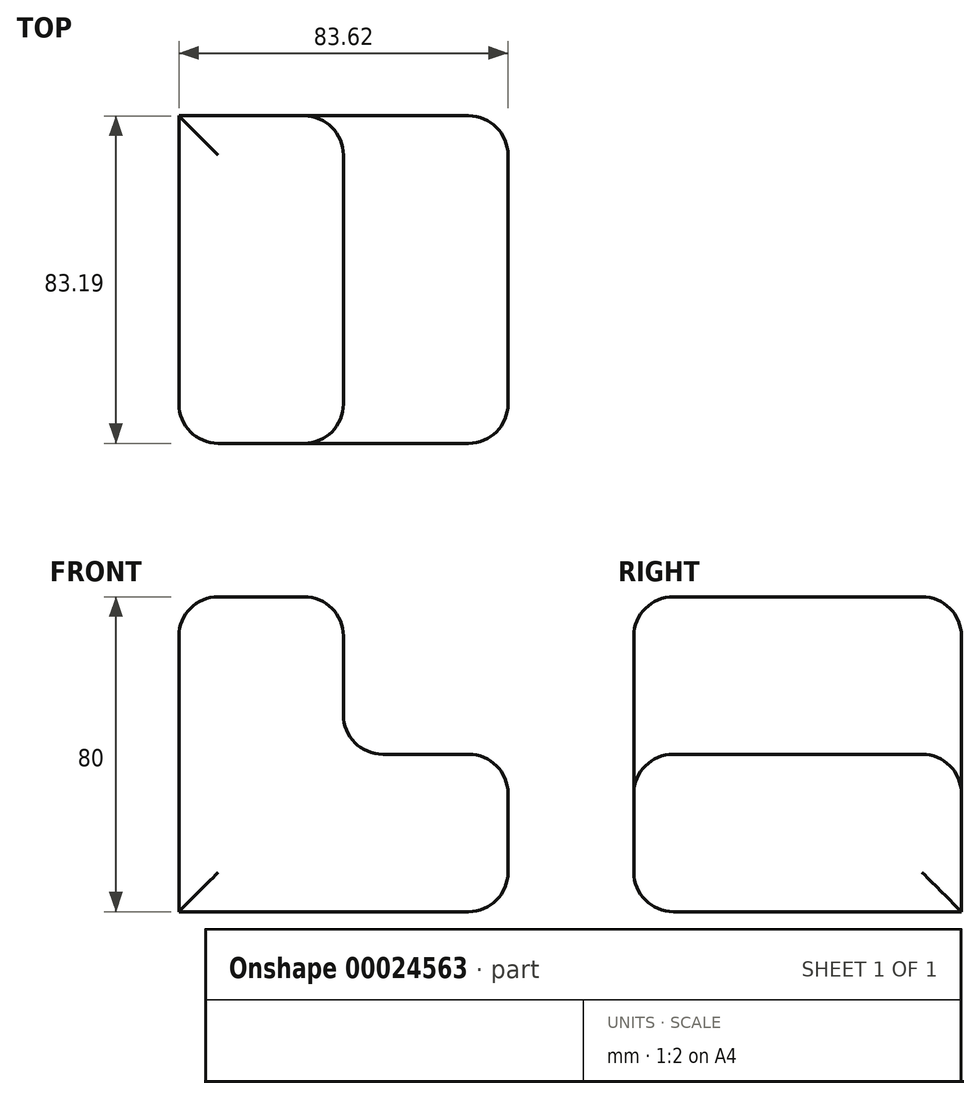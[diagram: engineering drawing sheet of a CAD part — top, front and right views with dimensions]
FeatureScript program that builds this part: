
annotation { "Feature Type Name" : "Feature", "Feature Type Description" : "" }
export const myFeature = defineFeature(function(context is Context, id is Id, definition is map)
    precondition{}
    {
        {
            var Q0;
            Q0=qCreatedBy(makeId("Top.planeOp"),FACE);
            var sketch = newSketch(context, id + "F0", { "sketchPlane" : qUnion([Q0])});
            skLineSegment(sketch, "E0.bottom", {"start": v(-59.13, -45.93) * mm, "end": v(24.5, -45.93) * mm});
            skLineSegment(sketch, "E0.top", {"start": v(-59.13, 37.26) * mm, "end": v(24.5, 37.26) * mm});
            skLineSegment(sketch, "E0.left", {"start": v(-59.13, -45.93) * mm, "end": v(-59.13, 37.26) * mm});
            skLineSegment(sketch, "E0.right", {"start": v(24.5, -45.93) * mm, "end": v(24.5, 37.26) * mm});
            skSolve(sketch);
        }
        {
            var Q0;
            Q0=makeQuery(id+"F0.imprint","IMPRINT",FACE,{"disambiguationData":[TD([[makeQuery(id+"F0.imprint","IMPRINT",EDGE,{"derivedFrom":sQuery(id+"F0.wireOp",EDGE,"E0.bottom")}),1.0]])]});
            extrude(context, id + "F1", {"entities" : qUnion([Q0]), "depth" : 40 * mm});
        }
        {
            var Q0;
            Q0=makeQuery(id+"F1.opExtrude","CAP_FACE",FACE,{"disambiguationData":[OSD([sQuery(id+"F0.wireOp",EDGE,"E0.bottom"),sQuery(id+"F0.wireOp",EDGE,"E0.top"),sQuery(id+"F0.wireOp",EDGE,"E0.left"),sQuery(id+"F0.wireOp",EDGE,"E0.right")])],"isStart":false});
            var sketch = newSketch(context, id + "F2", { "sketchPlane" : qUnion([Q0])});
            skLineSegment(sketch, "E1", {"start": v(-17.32, 37.26) * mm, "end": v(-17.32, -45.93) * mm});
            skSolve(sketch);
        }
        {
            var Q0;
            {var subQ1=sQuery(id+"F2.wireOp",EDGE,"E1");Q0=makeQuery(id+"F2.imprint","IMPRINT",FACE,{"disambiguationData":[TD([[makeQuery(id+"F2.imprint","IMPRINT",EDGE,{"derivedFrom":subQ1}),-1.0]])]});}
            extrude(context, id + "F3", {"entities" : qUnion([Q0]), "operationType" : NewBodyOperationType.ADD, "depth" : 40 * mm});
        }
        {
            var Q0;
            Q0=makeQuery(id+"F3.opExtrude","CAP_FACE",FACE,{"disambiguationData":[OSD([sQuery(id+"F0.wireOp",EDGE,"E0.bottom"),sQuery(id+"F0.wireOp",EDGE,"E0.top"),sQuery(id+"F0.wireOp",EDGE,"E0.left"),sQuery(id+"F2.wireOp",EDGE,"E1")])],"isStart":false});
            var Q1;
            Q1=makeQuery(id+"F3.opExtrude","SWEPT_FACE",FACE,{"disambiguationData":[OSD([sQuery(id+"F2.wireOp",EDGE,"E1")])]});
            var Q2;
            Q2=makeQuery(id+"F1.opExtrude","CAP_FACE",FACE,{"disambiguationData":[OSD([sQuery(id+"F0.wireOp",EDGE,"E0.bottom"),sQuery(id+"F0.wireOp",EDGE,"E0.top"),sQuery(id+"F0.wireOp",EDGE,"E0.left"),sQuery(id+"F0.wireOp",EDGE,"E0.right")])],"isStart":false});
            var Q3;
            {var subQ0=sQuery(id+"F0.wireOp",EDGE,"E0.bottom");Q3=makeQuery(id+"F3.boolean.opBoolean","MERGE",FACE,{"derivedFrom":[makeQuery(id+"F1.opExtrude","SWEPT_FACE",FACE,{"disambiguationData":[OSD([subQ0])]}),makeQuery(id+"F3.opExtrude","SWEPT_FACE",FACE,{"disambiguationData":[OSD([subQ0])]})]});}
            var Q4;
            Q4=makeQuery(id+"F1.opExtrude","SWEPT_FACE",FACE,{"disambiguationData":[OSD([sQuery(id+"F0.wireOp",EDGE,"E0.right")])]});
            fillet(context, id + "F4", {"entities" : qUnion([Q0, Q1, Q2, Q3, Q4]), "radius" : 10 * mm, "tangentPropagation" : true, "allowEdgeOverflow" : false});
        }
    });
